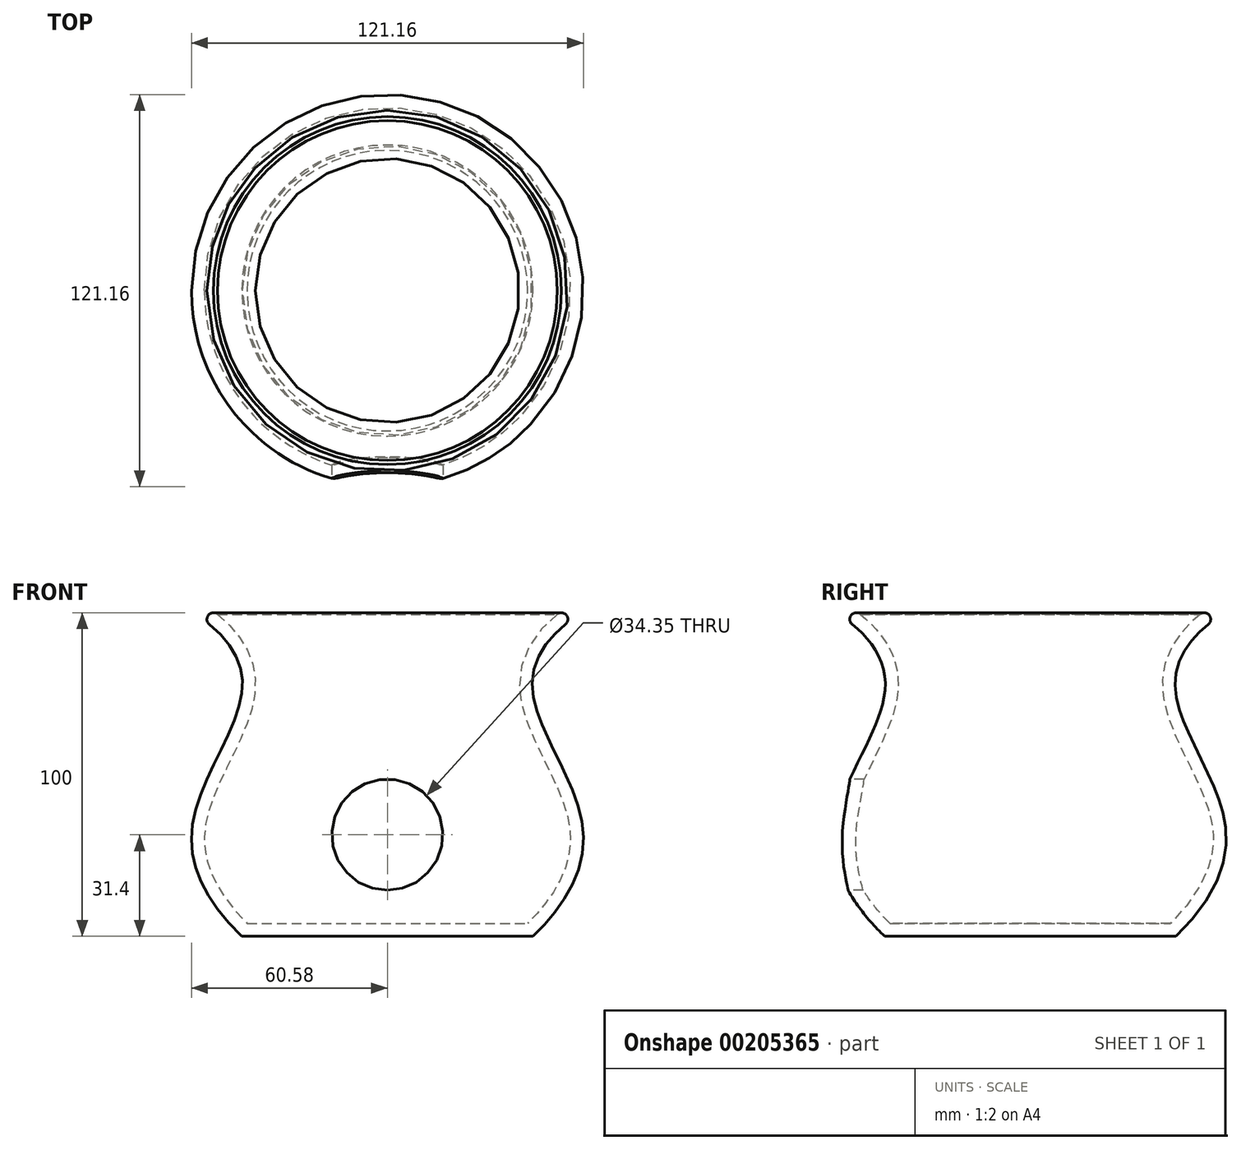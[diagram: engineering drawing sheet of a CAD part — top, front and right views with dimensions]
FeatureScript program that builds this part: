
annotation { "Feature Type Name" : "Feature", "Feature Type Description" : "" }
export const myFeature = defineFeature(function(context is Context, id is Id, definition is map)
    precondition{}
    {
        {
            var Q0;
            Q0=qCreatedBy(makeId("Front.planeOp"),FACE);
            var sketch = newSketch(context, id + "F0", { "sketchPlane" : qUnion([Q0])});
            skLineSegment(sketch, "E0.bottom", {"start": v(0, 0) * mm, "end": v(-60, 0) * mm});
            skLineSegment(sketch, "E0.top", {"start": v(0, 100) * mm, "end": v(-60, 100) * mm});
            skLineSegment(sketch, "E0.left", {"start": v(0, 0) * mm, "end": v(0, 100) * mm});
            skFitSpline(sketch, "E1", {"points": [v(-60, 100) * mm, v(-45, 75) * mm, v(-60, 36.15) * mm, v(-45, 0) * mm], "startDerivative": vector(112.08, -71.75) * mm, "endDerivative": vector(104.92, -101.33) * mm});
            skSolve(sketch);
        }
        {
            var Q0;
            Q0=makeQuery(id+"F0.imprint","IMPRINT",FACE,{"disambiguationData":[TD([[makeQuery(id+"F0.imprint","IMPRINT",EDGE,{"derivedFrom":sQuery(id+"F0.wireOp",EDGE,"E0.top")}),1.0]])]});
            var Q1;
            Q1=sQuery(id+"F0.wireOp",EDGE,"E0.left");
            revolve(context, id + "F1", {"entities" : qUnion([Q0]), "axis" : qUnion([Q1]), "revolveType" : RevolveType.FULL});
        }
        {
            var Q0;
            Q0=makeQuery(id+"F1.opRevolve","SWEPT_FACE",FACE,{"disambiguationData":[OSD([sQuery(id+"F0.wireOp",EDGE,"E0.top")])]});
            shell(context, id + "F2", {"entities" : qUnion([Q0]), "thickness" : 4 * mm});
        }
        {
            var Q0;
            Q0=makeQuery(id+"F1.opRevolve","SWEPT_EDGE",EDGE,{"disambiguationData":[OSD([sQuery(id+"F0.wireOp",EDGE,"E0.top"),sQuery(id+"F0.wireOp",EDGE,"E1")])]});
            fillet(context, id + "F3", {"entities" : qUnion([Q0]), "radius" : 2 * mm, "tangentPropagation" : true, "allowEdgeOverflow" : false});
        }
        {
            var Q0;
            Q0=makeQuery(id+"F2.opShell","OFFSET_EDGE",EDGE,{"disambiguationData":[OSD([sQuery(id+"F0.wireOp",EDGE,"E0.top"),sQuery(id+"F0.wireOp",EDGE,"E1")])]});
            chamfer(context, id + "F4", {"entities" : qUnion([Q0]), "width" : 2 * mm, "tangentPropagation" : true});
        }
        {
            var Q0;
            Q0=qCreatedBy(makeId("Front.planeOp"),FACE);
            cPlane(context, id + "F5", {"entities" : qUnion([Q0]), "cplaneType" : CPlaneType.OFFSET, "offset" : 80 * mm, "width" : 150 * mm, "height" : 150 * mm});
        }
        {
            var Q0;
            Q0=qCreatedBy(id+"F5.planeOp",FACE);
            var sketch = newSketch(context, id + "F6", { "sketchPlane" : qUnion([Q0])});
            skCircle(sketch, "E2", {"center": v(0, 31.4) * mm, "radius": 17.17 * mm});
            skSolve(sketch);
        }
        {
            var Q0;
            Q0=makeQuery(id+"F6.imprint","IMPRINT",FACE,{"disambiguationData":[TD([[makeQuery(id+"F6.imprint","IMPRINT",EDGE,{"derivedFrom":sQuery(id+"F6.wireOp",EDGE,"E2")}),1.0]])]});
            extrude(context, id + "F7", {"entities" : qUnion([Q0]), "operationType" : NewBodyOperationType.REMOVE, "oppositeDirection" : true, "depth" : 80 * mm});
        }
    });
